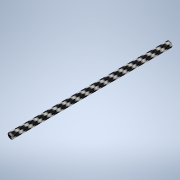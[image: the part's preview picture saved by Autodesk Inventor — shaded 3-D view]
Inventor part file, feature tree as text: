
AUTODESK INVENTOR PART (.ipt)
format: ipt  version: 2020 (Build 240168000, 168)  size: 109,056 bytes
history: native  units: in
note: dims shown in document units (in); Inventor stores cm internally (conversion verified against a paired STEP export)
features: extrude x1, sketch x1
ambient origin geometry x8: Origin, YZ Plane, XZ Plane, XY Plane, X Axis, Y Axis, Z Axis, Center Point
bodies: Solid1 (feature_tree)
feature tree (2):
  extrude  "Extrusion1"  Depth=2.4807in
  sketch  "Sketch1"  dims[d0=0.0906in d1=2.4807in d2=0.0in]
